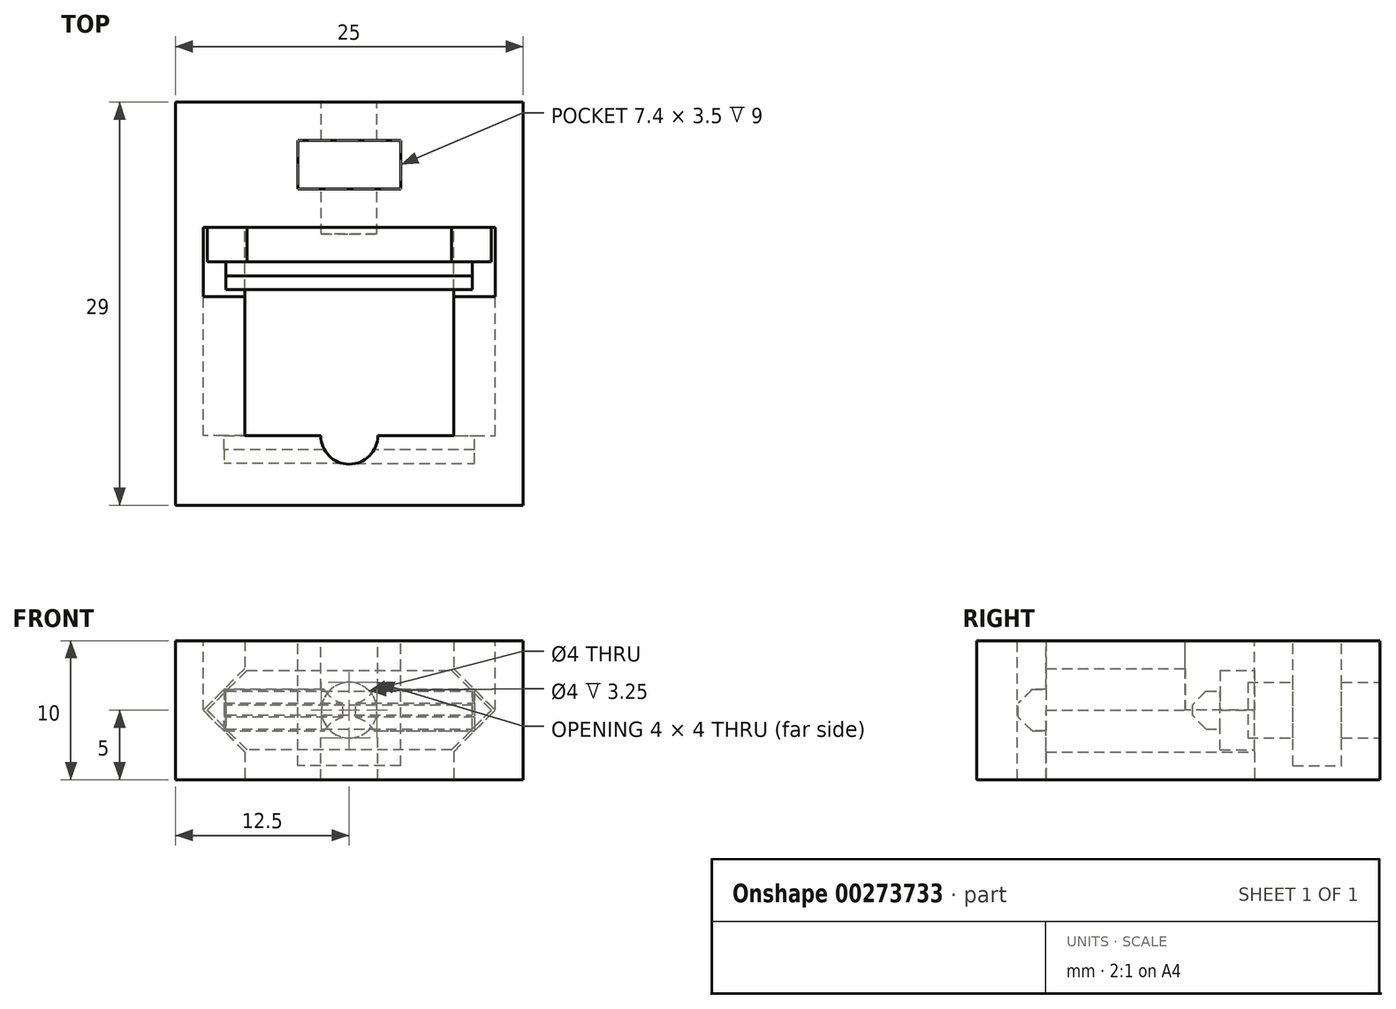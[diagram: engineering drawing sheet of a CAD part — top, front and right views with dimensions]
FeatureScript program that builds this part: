
annotation { "Feature Type Name" : "Feature", "Feature Type Description" : "" }
export const myFeature = defineFeature(function(context is Context, id is Id, definition is map)
    precondition{}
    {
        {
            var Q0;
            Q0=qCreatedBy(makeId("Top.planeOp"),FACE);
            var sketch = newSketch(context, id + "F0", { "sketchPlane" : qUnion([Q0])});
            skLineSegment(sketch, "E0.bottom", {"start": v(-20, 20) * mm, "end": v(-5, 20) * mm});
            skLineSegment(sketch, "E0.top", {"start": v(-20, 5) * mm, "end": v(-5, 5) * mm});
            skLineSegment(sketch, "E0.left", {"start": v(-20, 20) * mm, "end": v(-20, 5) * mm});
            skLineSegment(sketch, "E0.right", {"start": v(-5, 20) * mm, "end": v(-5, 5) * mm});
            skLineSegment(sketch, "E1.0", {"start": v(-25, 25) * mm, "end": v(-25, 0) * mm});
            skLineSegment(sketch, "E1.1", {"start": v(-25, 25) * mm, "end": v(0, 25) * mm});
            skLineSegment(sketch, "E1.2", {"start": v(0, 25) * mm, "end": v(0, 0) * mm});
            skLineSegment(sketch, "E1.3", {"start": v(-25, 0) * mm, "end": v(0, 0) * mm});
            skLineSegment(sketch, "E2", {"start": v(-25, 25) * mm, "end": v(-25, 29) * mm});
            skLineSegment(sketch, "E3", {"start": v(-25, 29) * mm, "end": v(0, 29) * mm});
            skLineSegment(sketch, "E4", {"start": v(0, 29) * mm, "end": v(0, 25) * mm});
            skSolve(sketch);
        }
        {
            var Q0;
            Q0=makeQuery(id+"F0.imprint","IMPRINT",FACE,{"disambiguationData":[TD([[makeQuery(id+"F0.imprint","IMPRINT",EDGE,{"derivedFrom":sQuery(id+"F0.wireOp",EDGE,"E0.bottom")}),1.0]])]});
            var Q1;
            Q1=makeQuery(id+"F0.imprint","IMPRINT",FACE,{"disambiguationData":[TD([[makeQuery(id+"F0.imprint","IMPRINT",EDGE,{"derivedFrom":sQuery(id+"F0.wireOp",EDGE,"E1.1")}),1.0]])]});
            extrude(context, id + "F1", {"entities" : qUnion([Q0, Q1]), "depth" : 10 * mm, "offsetDistance" : 25 * mm});
        }
        {
            var Q0;
            Q0=makeQuery(id+"F1.opExtrude","CAP_FACE",FACE,{"disambiguationData":[OSD([sQuery(id+"F0.wireOp",EDGE,"E0.bottom"),sQuery(id+"F0.wireOp",EDGE,"E0.top"),sQuery(id+"F0.wireOp",EDGE,"E0.left"),sQuery(id+"F0.wireOp",EDGE,"E0.right"),sQuery(id+"F0.wireOp",EDGE,"E1.0"),sQuery(id+"F0.wireOp",EDGE,"E1.1"),sQuery(id+"F0.wireOp",EDGE,"E1.2"),sQuery(id+"F0.wireOp",EDGE,"E1.3")])],"isStart":false});
            var sketch = newSketch(context, id + "F2", { "sketchPlane" : qUnion([Q0])});
            skLineSegment(sketch, "E5.bottom", {"start": v(-23, 20) * mm, "end": v(-2, 20) * mm});
            skLineSegment(sketch, "E5.top", {"start": v(-23, 15) * mm, "end": v(-2, 15) * mm});
            skLineSegment(sketch, "E5.left", {"start": v(-23, 20) * mm, "end": v(-23, 15) * mm});
            skLineSegment(sketch, "E5.right", {"start": v(-2, 20) * mm, "end": v(-2, 15) * mm});
            skSolve(sketch);
        }
        {
            var Q0;
            {var subQ3=sQuery(id+"F2.wireOp",EDGE,"E5.left");Q0=makeQuery(id+"F2.imprint","IMPRINT",FACE,{"disambiguationData":[TD([[makeQuery(id+"F2.imprint","IMPRINT",EDGE,{"derivedFrom":subQ3}),1.0]])]});}
            var Q1;
            {var subQ3=sQuery(id+"F2.wireOp",EDGE,"E5.right");Q1=makeQuery(id+"F2.imprint","IMPRINT",FACE,{"disambiguationData":[TD([[makeQuery(id+"F2.imprint","IMPRINT",EDGE,{"derivedFrom":subQ3}),-1.0]])]});}
            extrude(context, id + "F3", {"entities" : qUnion([Q0, Q1]), "operationType" : NewBodyOperationType.REMOVE, "oppositeDirection" : true, "depth" : 5 * mm, "offsetDistance" : 25 * mm});
        }
        {
            var Q0;
            {var subQ0=sQuery(id+"F2.wireOp",EDGE,"E5.top");Q0=makeQuery(id+"F3.boolean.opBoolean","COPY",FACE,{"derivedFrom":makeQuery(id+"F3.opExtrude","SWEPT_FACE",FACE,{"disambiguationData":[OSD([subQ0]),TDD([makeQuery(id+"F2.imprint","IMPRINT",EDGE,{"disambiguationData":[TD([[makeQuery(id+"F2.imprint","INTERSECT",VERTEX,{"derivedFrom":[subQ0,sQuery(id+"F2.wireOp",EDGE,"E5.right")]}),1.0]])],"derivedFrom":subQ0})])]})});}
            var sketch = newSketch(context, id + "F4", { "sketchPlane" : qUnion([Q0])});
            skLineSegment(sketch, "E6", {"start": v(2, 5) * mm, "end": v(5, 2) * mm});
            skLineSegment(sketch, "E7", {"start": v(23, 5) * mm, "end": v(20, 2) * mm});
            skLineSegment(sketch, "E8.0", {"start": v(20, 5) * mm, "end": v(20, 0) * mm});
            skLineSegment(sketch, "E9.0", {"start": v(23, 5) * mm, "end": v(20, 5) * mm});
            skLineSegment(sketch, "E10", {"start": v(5, 2) * mm, "end": v(5, 5) * mm});
            skLineSegment(sketch, "E11", {"start": v(2, 5) * mm, "end": v(5, 8) * mm});
            skLineSegment(sketch, "E12", {"start": v(23, 5) * mm, "end": v(20, 8) * mm});
            skLineSegment(sketch, "E13.0", {"start": v(20, 5) * mm, "end": v(20, 10) * mm});
            skSolve(sketch);
        }
        {
            var Q0;
            Q0 = qSketchRegion(id + "F4", true);
            var Q1;
            Q1=makeQuery(id+"F4.imprint","IMPRINT",FACE,{"disambiguationData":[TD([[makeQuery(id+"F4.imprint","IMPRINT",EDGE,{"derivedFrom":sQuery(id+"F4.wireOp",EDGE,"E6")}),1.0]])]});
            var Q2;
            {var subQ0=sQuery(id+"F4.wireOp",EDGE,"E11");Q2=makeQuery(id+"F4.imprint","IMPRINT",FACE,{"disambiguationData":[TD([[makeQuery(id+"F4.imprint","IMPRINT",EDGE,{"derivedFrom":subQ0}),-1.0]])]});}
            var Q3;
            Q3=makeQuery(id+"F1.opExtrude","SWEPT_FACE",FACE,{"disambiguationData":[OSD([sQuery(id+"F0.wireOp",EDGE,"E0.top")])]});
            var Q4;
            {var subQ0=sQuery(id+"F2.wireOp",EDGE,"E5.bottom");Q4=makeQuery(id+"F3.boolean.opBoolean","MERGE",FACE,{"derivedFrom":[makeQuery(id+"F1.opExtrude","SWEPT_FACE",FACE,{"disambiguationData":[OSD([sQuery(id+"F0.wireOp",EDGE,"E0.bottom")])]})],"fromTools":[makeQuery(id+"F3.opExtrude","SWEPT_FACE",FACE,{"disambiguationData":[OSD([subQ0]),TDD([makeQuery(id+"F2.imprint","IMPRINT",EDGE,{"disambiguationData":[TD([[makeQuery(id+"F2.imprint","INTERSECT",VERTEX,{"derivedFrom":[makeQuery(id+"F1.opExtrude","CAP_EDGE",EDGE,{"disambiguationData":[OSD([sQuery(id+"F0.wireOp",EDGE,"E0.left")])],"isStart":false}),subQ0]}),1.0]])],"derivedFrom":subQ0})])]}),makeQuery(id+"F3.opExtrude","SWEPT_FACE",FACE,{"disambiguationData":[OSD([subQ0]),TDD([makeQuery(id+"F2.imprint","IMPRINT",EDGE,{"disambiguationData":[TD([[makeQuery(id+"F2.imprint","INTERSECT",VERTEX,{"derivedFrom":[makeQuery(id+"F1.opExtrude","CAP_EDGE",EDGE,{"disambiguationData":[OSD([sQuery(id+"F0.wireOp",EDGE,"E0.right")])],"isStart":false}),subQ0]}),-1.0]])],"derivedFrom":subQ0})])]})]});}
            extrude(context, id + "F5", {"entities" : qUnion([Q0, Q1, Q2]), "operationType" : NewBodyOperationType.REMOVE, "endBound" : BoundingType.UP_TO_SURFACE, "oppositeDirection" : true, "depth" : 25 * mm, "endBoundEntityFace" : qUnion([Q3]), "offsetDistance" : 25 * mm, "hasSecondDirection" : true, "secondDirectionBound" : SecondDirectionBoundingType.UP_TO_SURFACE, "secondDirectionOppositeDirection" : false, "secondDirectionDepth" : 25 * mm, "secondDirectionBoundEntityFace" : qUnion([Q4])});
        }
        {
            var Q0;
            {var subQ0=sQuery(id+"F0.wireOp",EDGE,"E0.left");var subQ1=sQuery(id+"F4.wireOp",EDGE,"E12");var subQ6=sQuery(id+"F0.wireOp",EDGE,"E0.right");var subQ7=sQuery(id+"F0.wireOp",EDGE,"E0.top");var subQ9=sQuery(id+"F4.wireOp",EDGE,"E7");Q0=makeQuery(id+"F10.boolean.opBoolean","SPLIT",FACE,{"disambiguationData":[TD([makeQuery(id+"F1.opExtrude","SWEPT_FACE",FACE,{"disambiguationData":[OSD([subQ0])]})])],"derivedFrom":makeQuery(id+"F5.boolean.opBoolean","MERGE",FACE,{"derivedFrom":[makeQuery(id+"F1.opExtrude","SWEPT_FACE",FACE,{"disambiguationData":[OSD([subQ7])]})],"fromTools":[makeQuery(id+"F5.opExtrude","CAP_FACE",FACE,{"disambiguationData":[OSD([subQ6,sQuery(id+"F2.wireOp",EDGE,"E5.top"),sQuery(id+"F4.wireOp",EDGE,"E6"),sQuery(id+"F4.wireOp",EDGE,"E10"),sQuery(id+"F4.wireOp",EDGE,"E11")])],"isStart":false}),makeQuery(id+"F5.opExtrude","CAP_FACE",FACE,{"disambiguationData":[OSD([subQ9,sQuery(id+"F4.wireOp",EDGE,"E8.0"),subQ1,sQuery(id+"F4.wireOp",EDGE,"E13.0")])],"isStart":false})]})});}
            var sketch = newSketch(context, id + "F6", { "sketchPlane" : qUnion([Q0])});
            skPoint(sketch, "E14.oppositeSnap0", {"position": v(21.5, 3.5) * mm});
            skLineSegment(sketch, "E14.bottom", {"start": v(21.5, 6.5) * mm, "end": v(3.5, 6.5) * mm});
            skLineSegment(sketch, "E14.top", {"start": v(21.5, 3.5) * mm, "end": v(3.5, 3.5) * mm});
            skLineSegment(sketch, "E14.left", {"start": v(21.5, 6.5) * mm, "end": v(21.5, 3.5) * mm});
            skLineSegment(sketch, "E14.right", {"start": v(3.5, 6.5) * mm, "end": v(3.5, 3.5) * mm});
            skLineSegment(sketch, "E15.0", {"start": v(5, 8) * mm, "end": v(2, 5) * mm});
            skSolve(sketch);
        }
        {
            var Q0;
            {var subQ0=sQuery(id+"F6.wireOp",EDGE,"E14.left");Q0=makeQuery(id+"F6.imprint","IMPRINT",FACE,{"disambiguationData":[TD([[makeQuery(id+"F6.imprint","IMPRINT",EDGE,{"derivedFrom":subQ0}),-1.0]])]});}
            var Q1;
            {var subQ0=sQuery(id+"F6.wireOp",EDGE,"E14.right");Q1=makeQuery(id+"F6.imprint","IMPRINT",FACE,{"disambiguationData":[TD([[makeQuery(id+"F6.imprint","IMPRINT",EDGE,{"derivedFrom":subQ0}),1.0]])]});}
            extrude(context, id + "F7", {"entities" : qUnion([Q0, Q1]), "operationType" : NewBodyOperationType.REMOVE, "oppositeDirection" : true, "depth" : 2 * mm, "offsetDistance" : 25 * mm});
        }
        {
            var Q0;
            {var subQ0=sQuery(id+"F6.wireOp",EDGE,"E14.left");var subQ1=sQuery(id+"F6.wireOp",EDGE,"E14.top");Q0=makeQuery(id+"F7.boolean.opBoolean","COPY",EDGE,{"disambiguationData":[TD([makeQuery(id+"F7.opExtrude","SWEPT_FACE",FACE,{"disambiguationData":[OSD([subQ0])]})])],"derivedFrom":makeQuery(id+"F7.opExtrude","CAP_EDGE",EDGE,{"disambiguationData":[OSD([subQ1])],"isStart":false})});}
            var Q1;
            {var subQ0=sQuery(id+"F6.wireOp",EDGE,"E14.left");var subQ1=sQuery(id+"F6.wireOp",EDGE,"E14.bottom");Q1=makeQuery(id+"F7.boolean.opBoolean","COPY",EDGE,{"disambiguationData":[TD([makeQuery(id+"F7.opExtrude","SWEPT_FACE",FACE,{"disambiguationData":[OSD([subQ0])]})])],"derivedFrom":makeQuery(id+"F7.opExtrude","CAP_EDGE",EDGE,{"disambiguationData":[OSD([subQ1])],"isStart":false})});}
            var Q2;
            {var subQ0=sQuery(id+"F6.wireOp",EDGE,"E14.right");var subQ1=sQuery(id+"F6.wireOp",EDGE,"E14.top");Q2=makeQuery(id+"F7.boolean.opBoolean","COPY",EDGE,{"disambiguationData":[TD([makeQuery(id+"F7.opExtrude","SWEPT_FACE",FACE,{"disambiguationData":[OSD([subQ0])]})])],"derivedFrom":makeQuery(id+"F7.opExtrude","CAP_EDGE",EDGE,{"disambiguationData":[OSD([subQ1])],"isStart":false})});}
            var Q3;
            {var subQ0=sQuery(id+"F6.wireOp",EDGE,"E14.right");var subQ1=sQuery(id+"F6.wireOp",EDGE,"E14.bottom");Q3=makeQuery(id+"F7.boolean.opBoolean","COPY",EDGE,{"disambiguationData":[TD([makeQuery(id+"F7.opExtrude","SWEPT_FACE",FACE,{"disambiguationData":[OSD([subQ0])]})])],"derivedFrom":makeQuery(id+"F7.opExtrude","CAP_EDGE",EDGE,{"disambiguationData":[OSD([subQ1])],"isStart":false})});}
            chamfer(context, id + "F8", {"entities" : qUnion([Q0, Q1, Q2, Q3]), "width" : 1 * mm, "tangentPropagation" : true});
        }
        {
            var Q0;
            Q0=makeQuery(id+"F1.opExtrude","CAP_FACE",FACE,{"disambiguationData":[OSD([sQuery(id+"F0.wireOp",EDGE,"E0.bottom"),sQuery(id+"F0.wireOp",EDGE,"E0.top"),sQuery(id+"F0.wireOp",EDGE,"E0.left"),sQuery(id+"F0.wireOp",EDGE,"E0.right"),sQuery(id+"F0.wireOp",EDGE,"E1.0"),sQuery(id+"F0.wireOp",EDGE,"E1.1"),sQuery(id+"F0.wireOp",EDGE,"E1.2"),sQuery(id+"F0.wireOp",EDGE,"E1.3")])],"isStart":false});
            var sketch = newSketch(context, id + "F9", { "sketchPlane" : qUnion([Q0])});
            skCircle(sketch, "E16", {"center": v(-12.5, 5) * mm, "radius": 2.05 * mm});
            skSolve(sketch);
        }
        {
            var Q0;
            {var subQ0=sQuery(id+"F9.wireOp",EDGE,"E16");var subQ1=makeQuery(id+"F1.opExtrude","CAP_EDGE",EDGE,{"disambiguationData":[OSD([sQuery(id+"F0.wireOp",EDGE,"E0.top")])],"isStart":false});var subQ2=makeQuery(id+"F9.imprint","INTERSECT",VERTEX,{"disambiguationData":[OD(0.0)],"derivedFrom":[subQ1,subQ0]});Q0=makeQuery(id+"F9.imprint","IMPRINT",FACE,{"disambiguationData":[TD([[makeQuery(id+"F9.imprint","IMPRINT",EDGE,{"disambiguationData":[TD([[subQ2,-1.0]])],"derivedFrom":subQ0}),1.0]])]});}
            extrude(context, id + "F10", {"entities" : qUnion([Q0]), "operationType" : NewBodyOperationType.REMOVE, "oppositeDirection" : true, "depth" : 25 * mm, "offsetDistance" : 25 * mm});
        }
        {
            var Q0;
            Q0=makeQuery(id+"F1.opExtrude","SWEPT_FACE",FACE,{"disambiguationData":[OSD([sQuery(id+"F0.wireOp",EDGE,"E3")])]});
            var sketch = newSketch(context, id + "F11", { "sketchPlane" : qUnion([Q0])});
            skPoint(sketch, "E17", {"position": v(12.5, 5) * mm});
            skPoint(sketch, "E17.positionSnap0", {"position": v(25, 5) * mm});
            skPoint(sketch, "E17.positionSnap1", {"position": v(12.5, 0) * mm});
            skCircle(sketch, "E18", {"center": v(12.5, 5) * mm, "radius": 2 * mm});
            skSolve(sketch);
        }
        {
            var Q0;
            Q0=makeQuery(id+"F11.imprint","IMPRINT",FACE,{"disambiguationData":[TD([[makeQuery(id+"F11.imprint","IMPRINT",EDGE,{"derivedFrom":sQuery(id+"F11.wireOp",EDGE,"E18")}),1.0]])]});
            var Q1;
            {var subQ0=sQuery(id+"F0.wireOp",EDGE,"E0.right");var subQ1=sQuery(id+"F2.wireOp",EDGE,"E5.bottom");Q1=makeQuery(id+"F5.boolean.opBoolean","MERGE",FACE,{"derivedFrom":[makeQuery(id+"F3.boolean.opBoolean","MERGE",FACE,{"derivedFrom":[makeQuery(id+"F1.opExtrude","SWEPT_FACE",FACE,{"disambiguationData":[OSD([sQuery(id+"F0.wireOp",EDGE,"E0.bottom")])]})],"fromTools":[makeQuery(id+"F3.opExtrude","SWEPT_FACE",FACE,{"disambiguationData":[OSD([subQ1]),TDD([makeQuery(id+"F2.imprint","IMPRINT",EDGE,{"disambiguationData":[TD([[makeQuery(id+"F2.imprint","INTERSECT",VERTEX,{"derivedFrom":[makeQuery(id+"F1.opExtrude","CAP_EDGE",EDGE,{"disambiguationData":[OSD([sQuery(id+"F0.wireOp",EDGE,"E0.left")])],"isStart":false}),subQ1]}),1.0]])],"derivedFrom":subQ1})])]}),makeQuery(id+"F3.opExtrude","SWEPT_FACE",FACE,{"disambiguationData":[OSD([subQ1]),TDD([makeQuery(id+"F2.imprint","IMPRINT",EDGE,{"disambiguationData":[TD([[makeQuery(id+"F2.imprint","INTERSECT",VERTEX,{"derivedFrom":[makeQuery(id+"F1.opExtrude","CAP_EDGE",EDGE,{"disambiguationData":[OSD([subQ0])],"isStart":false}),subQ1]}),-1.0]])],"derivedFrom":subQ1})])]})]})],"fromTools":[makeQuery(id+"F5.opExtrude","CAP_FACE",FACE,{"disambiguationData":[OSD([subQ0,sQuery(id+"F2.wireOp",EDGE,"E5.top"),sQuery(id+"F4.wireOp",EDGE,"E6"),sQuery(id+"F4.wireOp",EDGE,"E10"),sQuery(id+"F4.wireOp",EDGE,"E11")])],"isStart":true}),makeQuery(id+"F5.opExtrude","CAP_FACE",FACE,{"disambiguationData":[OSD([sQuery(id+"F4.wireOp",EDGE,"E7"),sQuery(id+"F4.wireOp",EDGE,"E8.0"),sQuery(id+"F4.wireOp",EDGE,"E12"),sQuery(id+"F4.wireOp",EDGE,"E13.0")])],"isStart":true})]});}
            extrude(context, id + "F12", {"entities" : qUnion([Q0]), "operationType" : NewBodyOperationType.REMOVE, "endBound" : BoundingType.UP_TO_SURFACE, "oppositeDirection" : true, "depth" : 25 * mm, "endBoundEntityFace" : qUnion([Q1]), "offsetDistance" : 25 * mm});
        }
        {
            var Q0;
            Q0=makeQuery(id+"F1.opExtrude","CAP_FACE",FACE,{"disambiguationData":[OSD([sQuery(id+"F0.wireOp",EDGE,"E0.bottom"),sQuery(id+"F0.wireOp",EDGE,"E0.top"),sQuery(id+"F0.wireOp",EDGE,"E0.left"),sQuery(id+"F0.wireOp",EDGE,"E0.right"),sQuery(id+"F0.wireOp",EDGE,"E1.0"),sQuery(id+"F0.wireOp",EDGE,"E1.1"),sQuery(id+"F0.wireOp",EDGE,"E1.2"),sQuery(id+"F0.wireOp",EDGE,"E1.3")])],"isStart":false});
            var sketch = newSketch(context, id + "F13", { "sketchPlane" : qUnion([Q0])});
            skLineSegment(sketch, "E19.bottom", {"start": v(-16.2, 26.25) * mm, "end": v(-8.8, 26.25) * mm});
            skLineSegment(sketch, "E19.top", {"start": v(-16.2, 22.75) * mm, "end": v(-8.8, 22.75) * mm});
            skLineSegment(sketch, "E19.left", {"start": v(-16.2, 26.25) * mm, "end": v(-16.2, 22.75) * mm});
            skLineSegment(sketch, "E19.right", {"start": v(-8.8, 26.25) * mm, "end": v(-8.8, 22.75) * mm});
            skPoint(sketch, "E20", {"position": v(-12.5, 24.5) * mm});
            skPoint(sketch, "E20.positionSnap0", {"position": v(-16.2, 24.5) * mm});
            skPoint(sketch, "E20.positionSnap1", {"position": v(-12.5, 26.25) * mm});
            skLineSegment(sketch, "E21", {"start": v(-12.5, 29) * mm, "end": v(-12.5, 20) * mm, "construction": true});
            skSolve(sketch);
        }
        {
            var Q0;
            Q0=makeQuery(id+"F13.imprint","IMPRINT",FACE,{"disambiguationData":[TD([[makeQuery(id+"F13.imprint","IMPRINT",EDGE,{"derivedFrom":sQuery(id+"F13.wireOp",EDGE,"E19.bottom")}),-1.0]])]});
            var Q1;
            Q1=makeQuery(id+"F1.opExtrude","CAP_FACE",FACE,{"disambiguationData":[OSD([sQuery(id+"F0.wireOp",EDGE,"E0.bottom"),sQuery(id+"F0.wireOp",EDGE,"E0.top"),sQuery(id+"F0.wireOp",EDGE,"E0.left"),sQuery(id+"F0.wireOp",EDGE,"E0.right"),sQuery(id+"F0.wireOp",EDGE,"E1.0"),sQuery(id+"F0.wireOp",EDGE,"E1.2"),sQuery(id+"F0.wireOp",EDGE,"E1.3"),sQuery(id+"F0.wireOp",EDGE,"E2"),sQuery(id+"F0.wireOp",EDGE,"E3"),sQuery(id+"F0.wireOp",EDGE,"E4")])],"isStart":true});
            extrude(context, id + "F14", {"entities" : qUnion([Q0]), "operationType" : NewBodyOperationType.REMOVE, "endBound" : BoundingType.UP_TO_SURFACE, "oppositeDirection" : true, "depth" : 25 * mm, "endBoundEntityFace" : qUnion([Q1]), "hasOffset" : true, "offsetDistance" : 1 * mm});
        }
        {
            var Q0;
            {var subQ0=sQuery(id+"F0.wireOp",EDGE,"E0.right");var subQ1=sQuery(id+"F2.wireOp",EDGE,"E5.bottom");Q0=makeQuery(id+"F5.boolean.opBoolean","MERGE",FACE,{"derivedFrom":[makeQuery(id+"F3.boolean.opBoolean","MERGE",FACE,{"derivedFrom":[makeQuery(id+"F1.opExtrude","SWEPT_FACE",FACE,{"disambiguationData":[OSD([sQuery(id+"F0.wireOp",EDGE,"E0.bottom")])]})],"fromTools":[makeQuery(id+"F3.opExtrude","SWEPT_FACE",FACE,{"disambiguationData":[OSD([subQ1]),TDD([makeQuery(id+"F2.imprint","IMPRINT",EDGE,{"disambiguationData":[TD([[makeQuery(id+"F2.imprint","INTERSECT",VERTEX,{"derivedFrom":[makeQuery(id+"F1.opExtrude","CAP_EDGE",EDGE,{"disambiguationData":[OSD([sQuery(id+"F0.wireOp",EDGE,"E0.left")])],"isStart":false}),subQ1]}),1.0]])],"derivedFrom":subQ1})])]}),makeQuery(id+"F3.opExtrude","SWEPT_FACE",FACE,{"disambiguationData":[OSD([subQ1]),TDD([makeQuery(id+"F2.imprint","IMPRINT",EDGE,{"disambiguationData":[TD([[makeQuery(id+"F2.imprint","INTERSECT",VERTEX,{"derivedFrom":[makeQuery(id+"F1.opExtrude","CAP_EDGE",EDGE,{"disambiguationData":[OSD([subQ0])],"isStart":false}),subQ1]}),-1.0]])],"derivedFrom":subQ1})])]})]})],"fromTools":[makeQuery(id+"F5.opExtrude","CAP_FACE",FACE,{"disambiguationData":[OSD([subQ0,sQuery(id+"F2.wireOp",EDGE,"E5.top"),sQuery(id+"F4.wireOp",EDGE,"E6"),sQuery(id+"F4.wireOp",EDGE,"E10"),sQuery(id+"F4.wireOp",EDGE,"E11")])],"isStart":true}),makeQuery(id+"F5.opExtrude","CAP_FACE",FACE,{"disambiguationData":[OSD([sQuery(id+"F4.wireOp",EDGE,"E7"),sQuery(id+"F4.wireOp",EDGE,"E8.0"),sQuery(id+"F4.wireOp",EDGE,"E12"),sQuery(id+"F4.wireOp",EDGE,"E13.0")])],"isStart":true})]});}
            var sketch = newSketch(context, id + "F15", { "sketchPlane" : qUnion([Q0])});
            skLineSegment(sketch, "E22.0", {"start": v(-19.86, 2.14) * mm, "end": v(-21.36, 3.64) * mm});
            skLineSegment(sketch, "E22.1", {"start": v(-21.36, 3.64) * mm, "end": v(-22.72, 5) * mm});
            skLineSegment(sketch, "E22.2", {"start": v(-21.36, 6.36) * mm, "end": v(-22.72, 5) * mm});
            skLineSegment(sketch, "E22.3", {"start": v(-19.86, 7.86) * mm, "end": v(-21.36, 6.36) * mm});
            skLineSegment(sketch, "E23.0", {"start": v(-5.14, 2.14) * mm, "end": v(-3.64, 3.64) * mm});
            skLineSegment(sketch, "E23.1", {"start": v(-3.64, 3.64) * mm, "end": v(-2.28, 5) * mm});
            skLineSegment(sketch, "E23.2", {"start": v(-3.64, 6.36) * mm, "end": v(-2.28, 5) * mm});
            skLineSegment(sketch, "E23.3", {"start": v(-5.14, 7.86) * mm, "end": v(-3.64, 6.36) * mm});
            skLineSegment(sketch, "E24", {"start": v(-19.86, 7.86) * mm, "end": v(-5.14, 7.86) * mm});
            skLineSegment(sketch, "E25", {"start": v(-5.14, 2.14) * mm, "end": v(-19.86, 2.14) * mm});
            skLineSegment(sketch, "E26", {"start": v(-21.36, 6.36) * mm, "end": v(-21.36, 3.64) * mm});
            skLineSegment(sketch, "E27", {"start": v(-3.64, 3.64) * mm, "end": v(-21.36, 3.64) * mm});
            skLineSegment(sketch, "E28", {"start": v(-3.64, 6.36) * mm, "end": v(-3.64, 3.64) * mm});
            skLineSegment(sketch, "E29", {"start": v(-3.64, 6.36) * mm, "end": v(-21.36, 6.36) * mm});
            skSolve(sketch);
        }
        {
            var Q0;
            {var subQ5=sQuery(id+"F15.wireOp",EDGE,"E22.3");Q0=makeQuery(id+"F15.imprint","IMPRINT",FACE,{"disambiguationData":[TD([[makeQuery(id+"F15.imprint","IMPRINT",EDGE,{"derivedFrom":subQ5}),1.0]])]});}
            var Q1;
            Q1=makeQuery(id+"F15.imprint","IMPRINT",FACE,{"disambiguationData":[TD([[makeQuery(id+"F15.imprint","IMPRINT",EDGE,{"derivedFrom":sQuery(id+"F15.wireOp",EDGE,"E22.1")}),-1.0]])]});
            var Q2;
            {var subQ0=sQuery(id+"F15.wireOp",EDGE,"E26");Q2=makeQuery(id+"F15.imprint","IMPRINT",FACE,{"disambiguationData":[TD([[makeQuery(id+"F15.imprint","IMPRINT",EDGE,{"derivedFrom":subQ0}),1.0]])]});}
            var Q3;
            {var subQ0=sQuery(id+"F15.wireOp",EDGE,"E28");Q3=makeQuery(id+"F15.imprint","IMPRINT",FACE,{"disambiguationData":[TD([[makeQuery(id+"F15.imprint","IMPRINT",EDGE,{"derivedFrom":subQ0}),-1.0]])]});}
            var Q4;
            {var subQ4=sQuery(id+"F15.wireOp",EDGE,"E22.0");Q4=makeQuery(id+"F15.imprint","IMPRINT",FACE,{"disambiguationData":[TD([[makeQuery(id+"F15.imprint","IMPRINT",EDGE,{"derivedFrom":subQ4}),-1.0]])]});}
            var Q5;
            Q5=makeQuery(id+"F15.imprint","IMPRINT",FACE,{"disambiguationData":[TD([[makeQuery(id+"F15.imprint","IMPRINT",EDGE,{"derivedFrom":sQuery(id+"F15.wireOp",EDGE,"E23.1")}),1.0]])]});
            var Q6;
            {var subQ0=sQuery(id+"F15.wireOp",EDGE,"E27");var subQ1=makeQuery(id+"F12.boolean.opBoolean","COPY",EDGE,{"derivedFrom":makeQuery(id+"F12.opExtrude","CAP_EDGE",EDGE,{"disambiguationData":[OSD([sQuery(id+"F11.wireOp",EDGE,"E18")])],"isStart":false})});var subQ2=makeQuery(id+"F15.imprint","INTERSECT",VERTEX,{"disambiguationData":[OD(0.0)],"derivedFrom":[subQ1,subQ0]});Q6=makeQuery(id+"F15.imprint","IMPRINT",FACE,{"disambiguationData":[TD([[makeQuery(id+"F15.imprint","IMPRINT",EDGE,{"disambiguationData":[TD([[subQ2,-1.0]])],"derivedFrom":subQ0}),-1.0]])]});}
            var Q7;
            {var subQ0=sQuery(id+"F15.wireOp",EDGE,"E27");var subQ1=makeQuery(id+"F12.boolean.opBoolean","COPY",EDGE,{"derivedFrom":makeQuery(id+"F12.opExtrude","CAP_EDGE",EDGE,{"disambiguationData":[OSD([sQuery(id+"F11.wireOp",EDGE,"E18")])],"isStart":false})});var subQ2=makeQuery(id+"F15.imprint","INTERSECT",VERTEX,{"disambiguationData":[OD(0.0)],"derivedFrom":[subQ1,subQ0]});Q7=makeQuery(id+"F15.imprint","IMPRINT",FACE,{"disambiguationData":[TD([[makeQuery(id+"F15.imprint","IMPRINT",EDGE,{"disambiguationData":[TD([[subQ2,-1.0]])],"derivedFrom":subQ0}),1.0]])]});}
            var Q8;
            {var subQ0=sQuery(id+"F15.wireOp",EDGE,"E29");var subQ1=makeQuery(id+"F12.boolean.opBoolean","COPY",EDGE,{"derivedFrom":makeQuery(id+"F12.opExtrude","CAP_EDGE",EDGE,{"disambiguationData":[OSD([sQuery(id+"F11.wireOp",EDGE,"E18")])],"isStart":false})});var subQ2=makeQuery(id+"F15.imprint","INTERSECT",VERTEX,{"disambiguationData":[OD(0.0)],"derivedFrom":[subQ1,subQ0]});Q8=makeQuery(id+"F15.imprint","IMPRINT",FACE,{"disambiguationData":[TD([[makeQuery(id+"F15.imprint","IMPRINT",EDGE,{"disambiguationData":[TD([[subQ2,-1.0]])],"derivedFrom":subQ0}),-1.0]])]});}
            extrude(context, id + "F16", {"entities" : qUnion([Q0, Q1, Q2, Q3, Q4, Q5, Q6, Q7, Q8]), "depth" : 2.5 * mm, "offsetDistance" : 25 * mm});
        }
        {
            var Q0;
            {var subQ0=sQuery(id+"F15.wireOp",EDGE,"E26");Q0=makeQuery(id+"F15.imprint","IMPRINT",FACE,{"disambiguationData":[TD([[makeQuery(id+"F15.imprint","IMPRINT",EDGE,{"derivedFrom":subQ0}),1.0]])]});}
            var Q1;
            {var subQ0=sQuery(id+"F15.wireOp",EDGE,"E28");Q1=makeQuery(id+"F15.imprint","IMPRINT",FACE,{"disambiguationData":[TD([[makeQuery(id+"F15.imprint","IMPRINT",EDGE,{"derivedFrom":subQ0}),-1.0]])]});}
            var Q2;
            {var subQ0=sQuery(id+"F15.wireOp",EDGE,"E27");var subQ1=makeQuery(id+"F12.boolean.opBoolean","COPY",EDGE,{"derivedFrom":makeQuery(id+"F12.opExtrude","CAP_EDGE",EDGE,{"disambiguationData":[OSD([sQuery(id+"F11.wireOp",EDGE,"E18")])],"isStart":false})});var subQ2=makeQuery(id+"F15.imprint","INTERSECT",VERTEX,{"disambiguationData":[OD(0.0)],"derivedFrom":[subQ1,subQ0]});Q2=makeQuery(id+"F15.imprint","IMPRINT",FACE,{"disambiguationData":[TD([[makeQuery(id+"F15.imprint","IMPRINT",EDGE,{"disambiguationData":[TD([[subQ2,-1.0]])],"derivedFrom":subQ0}),-1.0]])]});}
            var Q3;
            Q3=makeQuery(id+"F16.opExtrude","CAP_FACE",FACE,{"disambiguationData":[OSD([sQuery(id+"F15.wireOp",EDGE,"E22.0"),sQuery(id+"F15.wireOp",EDGE,"E22.1"),sQuery(id+"F15.wireOp",EDGE,"E22.2"),sQuery(id+"F15.wireOp",EDGE,"E22.3"),sQuery(id+"F15.wireOp",EDGE,"E23.0"),sQuery(id+"F15.wireOp",EDGE,"E23.1"),sQuery(id+"F15.wireOp",EDGE,"E23.2"),sQuery(id+"F15.wireOp",EDGE,"E23.3"),sQuery(id+"F15.wireOp",EDGE,"E24"),sQuery(id+"F15.wireOp",EDGE,"E25")])],"isStart":false});
            extrude(context, id + "F17", {"entities" : qUnion([Q0, Q1, Q2]), "operationType" : NewBodyOperationType.ADD, "endBound" : BoundingType.UP_TO_SURFACE, "depth" : 25 * mm, "endBoundEntityFace" : qUnion([Q3]), "hasOffset" : true, "offsetDistance" : 2 * mm, "offsetOppositeDirection" : true});
        }
        {
            var Q0;
            Q0=makeQuery(id+"F17.opExtrude","CAP_EDGE",EDGE,{"disambiguationData":[OSD([sQuery(id+"F15.wireOp",EDGE,"E27")])],"isStart":false});
            var Q1;
            Q1=makeQuery(id+"F17.opExtrude","CAP_EDGE",EDGE,{"disambiguationData":[OSD([sQuery(id+"F15.wireOp",EDGE,"E29")])],"isStart":false});
            chamfer(context, id + "F18", {"entities" : qUnion([Q0, Q1]), "width" : 1 * mm, "tangentPropagation" : true});
        }
        {
            var Q0;
            {var subQ0=sQuery(id+"F15.wireOp",EDGE,"E27");var subQ1=makeQuery(id+"F12.boolean.opBoolean","COPY",EDGE,{"derivedFrom":makeQuery(id+"F12.opExtrude","CAP_EDGE",EDGE,{"disambiguationData":[OSD([sQuery(id+"F11.wireOp",EDGE,"E18")])],"isStart":false})});var subQ2=makeQuery(id+"F15.imprint","INTERSECT",VERTEX,{"disambiguationData":[OD(0.0)],"derivedFrom":[subQ1,subQ0]});Q0=makeQuery(id+"F15.imprint","IMPRINT",FACE,{"disambiguationData":[TD([[makeQuery(id+"F15.imprint","IMPRINT",EDGE,{"disambiguationData":[TD([[subQ2,-1.0]])],"derivedFrom":subQ0}),-1.0]])]});}
            var Q1;
            {var subQ0=sQuery(id+"F15.wireOp",EDGE,"E27");var subQ1=makeQuery(id+"F12.boolean.opBoolean","COPY",EDGE,{"derivedFrom":makeQuery(id+"F12.opExtrude","CAP_EDGE",EDGE,{"disambiguationData":[OSD([sQuery(id+"F11.wireOp",EDGE,"E18")])],"isStart":false})});var subQ2=makeQuery(id+"F15.imprint","INTERSECT",VERTEX,{"disambiguationData":[OD(0.0)],"derivedFrom":[subQ1,subQ0]});Q1=makeQuery(id+"F15.imprint","IMPRINT",FACE,{"disambiguationData":[TD([[makeQuery(id+"F15.imprint","IMPRINT",EDGE,{"disambiguationData":[TD([[subQ2,-1.0]])],"derivedFrom":subQ0}),1.0]])]});}
            var Q2;
            {var subQ0=sQuery(id+"F15.wireOp",EDGE,"E29");var subQ1=makeQuery(id+"F12.boolean.opBoolean","COPY",EDGE,{"derivedFrom":makeQuery(id+"F12.opExtrude","CAP_EDGE",EDGE,{"disambiguationData":[OSD([sQuery(id+"F11.wireOp",EDGE,"E18")])],"isStart":false})});var subQ2=makeQuery(id+"F15.imprint","INTERSECT",VERTEX,{"disambiguationData":[OD(0.0)],"derivedFrom":[subQ1,subQ0]});Q2=makeQuery(id+"F15.imprint","IMPRINT",FACE,{"disambiguationData":[TD([[makeQuery(id+"F15.imprint","IMPRINT",EDGE,{"disambiguationData":[TD([[subQ2,-1.0]])],"derivedFrom":subQ0}),-1.0]])]});}
            extrude(context, id + "F19", {"entities" : qUnion([Q0, Q1, Q2]), "operationType" : NewBodyOperationType.REMOVE, "depth" : 0.5 * mm, "offsetDistance" : 25 * mm});
        }
    });
